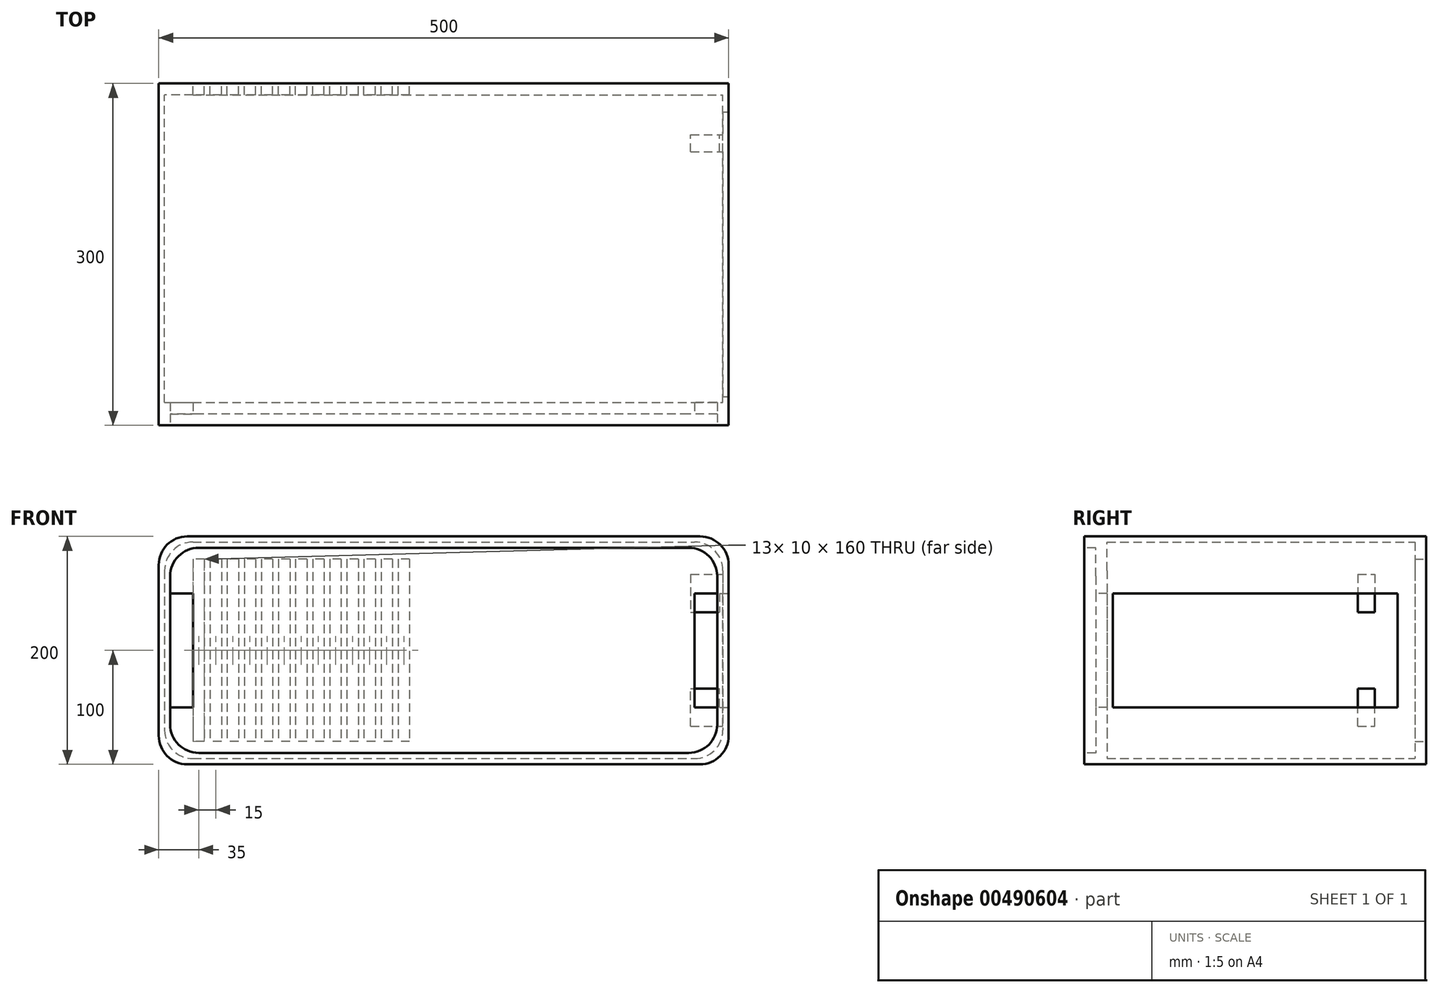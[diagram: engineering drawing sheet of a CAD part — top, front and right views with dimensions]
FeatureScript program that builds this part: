
annotation { "Feature Type Name" : "Feature", "Feature Type Description" : "" }
export const myFeature = defineFeature(function(context is Context, id is Id, definition is map)
    precondition{}
    {
        {
            var Q0;
            Q0=qCreatedBy(makeId("Front.planeOp"),FACE);
            var sketch = newSketch(context, id + "F0", { "sketchPlane" : qUnion([Q0])});
            skLineSegment(sketch, "E0.bottom", {"start": v(250, 100) * mm, "end": v(-250, 100) * mm});
            skLineSegment(sketch, "E0.top", {"start": v(250, -100) * mm, "end": v(-250, -100) * mm});
            skLineSegment(sketch, "E0.left", {"start": v(250, 100) * mm, "end": v(250, -100) * mm});
            skLineSegment(sketch, "E0.right", {"start": v(-250, 100) * mm, "end": v(-250, -100) * mm});
            skPoint(sketch, "E0.middle", {"position": v(0, 0) * mm});
            skSolve(sketch);
        }
        {
            var Q0;
            Q0=makeQuery(id+"F0.imprint","IMPRINT",FACE,{"disambiguationData":[TD([[makeQuery(id+"F0.imprint","IMPRINT",EDGE,{"derivedFrom":sQuery(id+"F0.wireOp",EDGE,"E0.bottom")}),1.0]])]});
            extrude(context, id + "F1", {"entities" : qUnion([Q0]), "endBound" : BoundingType.SYMMETRIC, "oppositeDirection" : true, "depth" : 300 * mm});
        }
        {
            var Q0;
            Q0=makeQuery(id+"F1.opExtrude","SWEPT_EDGE",EDGE,{"disambiguationData":[OSD([sQuery(id+"F0.wireOp",EDGE,"E0.bottom"),sQuery(id+"F0.wireOp",EDGE,"E0.right")])]});
            var Q1;
            Q1=makeQuery(id+"F1.opExtrude","SWEPT_EDGE",EDGE,{"disambiguationData":[OSD([sQuery(id+"F0.wireOp",EDGE,"E0.bottom"),sQuery(id+"F0.wireOp",EDGE,"E0.left")])]});
            var Q2;
            Q2=makeQuery(id+"F1.opExtrude","SWEPT_EDGE",EDGE,{"disambiguationData":[OSD([sQuery(id+"F0.wireOp",EDGE,"E0.top"),sQuery(id+"F0.wireOp",EDGE,"E0.left")])]});
            var Q3;
            Q3=makeQuery(id+"F1.opExtrude","SWEPT_EDGE",EDGE,{"disambiguationData":[OSD([sQuery(id+"F0.wireOp",EDGE,"E0.top"),sQuery(id+"F0.wireOp",EDGE,"E0.right")])]});
            fillet(context, id + "F2", {"entities" : qUnion([Q0, Q1, Q2, Q3]), "radius" : 25 * mm, "tangentPropagation" : true, "allowEdgeOverflow" : false});
        }
        {
            var Q0;
            Q0=makeQuery(id+"F1.opExtrude","CAP_FACE",FACE,{"disambiguationData":[OSD([sQuery(id+"F0.wireOp",EDGE,"E0.bottom"),sQuery(id+"F0.wireOp",EDGE,"E0.top"),sQuery(id+"F0.wireOp",EDGE,"E0.left"),sQuery(id+"F0.wireOp",EDGE,"E0.right")])],"isStart":true});
            var sketch = newSketch(context, id + "F3", { "sketchPlane" : qUnion([Q0])});
            skLineSegment(sketch, "E1.bottom", {"start": v(215, 90) * mm, "end": v(-215, 90) * mm});
            skLineSegment(sketch, "E1.top", {"start": v(215, -90) * mm, "end": v(-215, -90) * mm});
            skLineSegment(sketch, "E1.left", {"start": v(240, 65) * mm, "end": v(240, -65) * mm});
            skLineSegment(sketch, "E1.right", {"start": v(-240, 65) * mm, "end": v(-240, -65) * mm});
            skPoint(sketch, "E1.middle", {"position": v(0, 0) * mm});
            skPoint(sketch, "E2.visualSharp", {"position": v(-240, 90) * mm});
            skArc(sketch, "E2.filletArc", {"start": v(-215, 90) * mm, "mid": v(-232.68, 82.68) * mm, "end": v(-240, 65) * mm});
            skPoint(sketch, "E3.visualSharp", {"position": v(240, 90) * mm});
            skArc(sketch, "E3.filletArc", {"start": v(240, 65) * mm, "mid": v(232.68, 82.68) * mm, "end": v(215, 90) * mm});
            skPoint(sketch, "E4.visualSharp", {"position": v(240, -90) * mm});
            skArc(sketch, "E4.filletArc", {"start": v(215, -90) * mm, "mid": v(232.68, -82.68) * mm, "end": v(240, -65) * mm});
            skPoint(sketch, "E5.visualSharp", {"position": v(-240, -90) * mm});
            skArc(sketch, "E5.filletArc", {"start": v(-240, -65) * mm, "mid": v(-232.68, -82.68) * mm, "end": v(-215, -90) * mm});
            skSolve(sketch);
        }
        {
            var Q0;
            Q0=makeQuery(id+"F3.imprint","IMPRINT",FACE,{"disambiguationData":[TD([[makeQuery(id+"F3.imprint","IMPRINT",EDGE,{"derivedFrom":sQuery(id+"F3.wireOp",EDGE,"E1.bottom")}),1.0]])]});
            extrude(context, id + "F4", {"entities" : qUnion([Q0]), "operationType" : NewBodyOperationType.REMOVE, "oppositeDirection" : true, "depth" : 10 * mm});
        }
        {
            var Q0;
            Q0=makeQuery(id+"F1.opExtrude","CAP_FACE",FACE,{"disambiguationData":[OSD([sQuery(id+"F0.wireOp",EDGE,"E0.bottom"),sQuery(id+"F0.wireOp",EDGE,"E0.top"),sQuery(id+"F0.wireOp",EDGE,"E0.left"),sQuery(id+"F0.wireOp",EDGE,"E0.right")])],"isStart":false});
            var sketch = newSketch(context, id + "F5", { "sketchPlane" : qUnion([Q0])});
            skLineSegment(sketch, "E6.bottom", {"start": v(220, 95) * mm, "end": v(-220, 95) * mm});
            skLineSegment(sketch, "E6.top", {"start": v(220, -95) * mm, "end": v(-220, -95) * mm});
            skLineSegment(sketch, "E6.left", {"start": v(245, 70) * mm, "end": v(245, -70) * mm});
            skLineSegment(sketch, "E6.right", {"start": v(-245, 70) * mm, "end": v(-245, -70) * mm});
            skPoint(sketch, "E6.middle", {"position": v(0, 0) * mm});
            skPoint(sketch, "E7.visualSharp", {"position": v(-245, 95) * mm});
            skArc(sketch, "E7.filletArc", {"start": v(-220, 95) * mm, "mid": v(-237.68, 87.68) * mm, "end": v(-245, 70) * mm});
            skPoint(sketch, "E8.visualSharp", {"position": v(245, 95) * mm});
            skArc(sketch, "E8.filletArc", {"start": v(245, 70) * mm, "mid": v(237.68, 87.68) * mm, "end": v(220, 95) * mm});
            skPoint(sketch, "E9.visualSharp", {"position": v(245, -95) * mm});
            skArc(sketch, "E9.filletArc", {"start": v(220, -95) * mm, "mid": v(237.68, -87.68) * mm, "end": v(245, -70) * mm});
            skPoint(sketch, "E10.visualSharp", {"position": v(-245, -95) * mm});
            skArc(sketch, "E10.filletArc", {"start": v(-245, -70) * mm, "mid": v(-237.68, -87.68) * mm, "end": v(-220, -95) * mm});
            skSolve(sketch);
        }
        {
            var Q0;
            Q0=makeQuery(id+"F5.imprint","IMPRINT",FACE,{"disambiguationData":[TD([[makeQuery(id+"F5.imprint","IMPRINT",EDGE,{"derivedFrom":sQuery(id+"F5.wireOp",EDGE,"E6.bottom")}),1.0]])]});
            extrude(context, id + "F6", {"entities" : qUnion([Q0]), "operationType" : NewBodyOperationType.REMOVE, "oppositeDirection" : true, "depth" : 280 * mm});
        }
        {
            var Q0;
            {var subQ0=sQuery(id+"F3.wireOp",EDGE,"E5.filletArc");var subQ1=sQuery(id+"F3.wireOp",EDGE,"E1.right");var subQ2=sQuery(id+"F3.wireOp",EDGE,"E4.filletArc");var subQ3=sQuery(id+"F3.wireOp",EDGE,"E1.left");var subQ4=sQuery(id+"F3.wireOp",EDGE,"E3.filletArc");var subQ5=sQuery(id+"F3.wireOp",EDGE,"E2.filletArc");var subQ6=sQuery(id+"F3.wireOp",EDGE,"E1.top");var subQ7=sQuery(id+"F3.wireOp",EDGE,"E1.bottom");Q0=makeQuery(id+"FLLnC6cUkQxxpey_1.boolean.opBoolean","SPLIT",FACE,{"disambiguationData":[TD([makeQuery(id+"F4.boolean.opBoolean","COPY",FACE,{"derivedFrom":makeQuery(id+"F4.opExtrude","SWEPT_FACE",FACE,{"disambiguationData":[OSD([subQ7])]})})])],"derivedFrom":makeQuery(id+"F4.boolean.opBoolean","COPY",FACE,{"derivedFrom":makeQuery(id+"F4.opExtrude","CAP_FACE",FACE,{"disambiguationData":[OSD([subQ7,subQ6,subQ3,subQ1,subQ5,subQ4,subQ2,subQ0])],"isStart":false})})});}
            var sketch = newSketch(context, id + "F7", { "sketchPlane" : qUnion([Q0])});
            skLineSegment(sketch, "E11.bottom", {"start": v(240, 50) * mm, "end": v(220, 50) * mm});
            skLineSegment(sketch, "E11.top", {"start": v(240, -50) * mm, "end": v(220, -50) * mm});
            skLineSegment(sketch, "E11.left", {"start": v(240, 50) * mm, "end": v(240, -50) * mm});
            skLineSegment(sketch, "E11.right", {"start": v(220, 50) * mm, "end": v(220, -50) * mm});
            skLineSegment(sketch, "E12.MirrorCS", {"start": v(-240, -50) * mm, "end": v(-220, -50) * mm});
            skLineSegment(sketch, "E13.MirrorCS", {"start": v(-240, 50) * mm, "end": v(-220, 50) * mm});
            skLineSegment(sketch, "E14.MirrorCS", {"start": v(-240, 50) * mm, "end": v(-240, -50) * mm});
            skLineSegment(sketch, "E15.MirrorCS", {"start": v(-220, 50) * mm, "end": v(-220, -50) * mm});
            skSolve(sketch);
        }
        {
            var Q0;
            Q0=makeQuery(id+"F7.imprint","IMPRINT",FACE,{"disambiguationData":[TD([[makeQuery(id+"F7.imprint","IMPRINT",EDGE,{"derivedFrom":sQuery(id+"F7.wireOp",EDGE,"E12.MirrorCS")}),1.0]])]});
            var Q1;
            Q1=makeQuery(id+"F7.imprint","IMPRINT",FACE,{"disambiguationData":[TD([[makeQuery(id+"F7.imprint","IMPRINT",EDGE,{"derivedFrom":sQuery(id+"F7.wireOp",EDGE,"E11.bottom")}),1.0]])]});
            extrude(context, id + "F8", {"entities" : qUnion([Q0, Q1]), "operationType" : NewBodyOperationType.REMOVE, "endBound" : BoundingType.UP_TO_NEXT, "oppositeDirection" : true, "depth" : 25 * mm});
        }
        {
            var Q0;
            Q0=makeQuery(id+"F1.opExtrude","SWEPT_FACE",FACE,{"disambiguationData":[OSD([sQuery(id+"F0.wireOp",EDGE,"E0.bottom")])]});
            var sketch = newSketch(context, id + "F9", { "sketchPlane" : qUnion([Q0])});
            skLineSegment(sketch, "E16.bottom", {"start": v(-250, 140) * mm, "end": v(250, 140) * mm});
            skLineSegment(sketch, "E16.left", {"start": v(-250, 140) * mm, "end": v(-250, 150) * mm});
            skLineSegment(sketch, "E16.right", {"start": v(250, 140) * mm, "end": v(250, 150) * mm});
            skPoint(sketch, "E16.middle", {"position": v(0, 150) * mm});
            skLineSegment(sketch, "E17", {"start": v(-250, 150) * mm, "end": v(250, 150) * mm});
            skSolve(sketch);
        }
        {
            var Q0;
            {var subQ0=sQuery(id+"F9.wireOp",EDGE,"E16.left");Q0=makeQuery(id+"F9.imprint","IMPRINT",FACE,{"disambiguationData":[TD([[makeQuery(id+"F9.imprint","IMPRINT",EDGE,{"derivedFrom":subQ0}),-1.0]])]});}
            var Q1;
            {var subQ0=sQuery(id+"F9.wireOp",EDGE,"E16.bottom");var subQ1=sQuery(id+"F0.wireOp",EDGE,"E0.bottom");var subQ2=makeQuery(id+"F1.opExtrude","SWEPT_FACE",FACE,{"disambiguationData":[OSD([subQ1])]});var subQ3=makeQuery(id+"F2.opFillet","BLEND_EDGE",EDGE,{"blendedFrom":[makeQuery(id+"F1.opExtrude","SWEPT_EDGE",EDGE,{"disambiguationData":[OSD([subQ1,sQuery(id+"F0.wireOp",EDGE,"E0.right")])]}),subQ2],"blendedInto":[subQ2]});var subQ4=makeQuery(id+"F9.imprint","INTERSECT",VERTEX,{"derivedFrom":[subQ3,subQ0]});Q1=makeQuery(id+"F9.imprint","IMPRINT",FACE,{"disambiguationData":[TD([[makeQuery(id+"F9.imprint","IMPRINT",EDGE,{"disambiguationData":[TD([[subQ4,-1.0]])],"derivedFrom":subQ0}),1.0]])]});}
            var Q2;
            {var subQ0=sQuery(id+"F9.wireOp",EDGE,"E16.right");Q2=makeQuery(id+"F9.imprint","IMPRINT",FACE,{"disambiguationData":[TD([[makeQuery(id+"F9.imprint","IMPRINT",EDGE,{"derivedFrom":subQ0}),1.0]])]});}
            var Q3;
            Q3=makeQuery(id+"F1.opExtrude","SWEPT_FACE",FACE,{"disambiguationData":[OSD([sQuery(id+"F0.wireOp",EDGE,"E0.top")])]});
            extrude(context, id + "F10", {"entities" : qUnion([Q0, Q1, Q2]), "operationType" : NewBodyOperationType.ADD, "endBound" : BoundingType.UP_TO_SURFACE, "oppositeDirection" : true, "endBoundEntityFace" : qUnion([Q3]), "depth" : 25 * mm});
        }
        {
            var Q0;
            Q0=makeQuery(id+"F10.opExtrude","CAP_EDGE",EDGE,{"disambiguationData":[OSD([sQuery(id+"F9.wireOp",EDGE,"E16.left")])],"isStart":true});
            var Q1;
            Q1=makeQuery(id+"F10.opExtrude","CAP_EDGE",EDGE,{"disambiguationData":[OSD([sQuery(id+"F9.wireOp",EDGE,"E16.left")])],"isStart":false});
            var Q2;
            Q2=makeQuery(id+"F10.opExtrude","CAP_EDGE",EDGE,{"disambiguationData":[OSD([sQuery(id+"F9.wireOp",EDGE,"E16.right")])],"isStart":true});
            var Q3;
            Q3=makeQuery(id+"F10.opExtrude","CAP_EDGE",EDGE,{"disambiguationData":[OSD([sQuery(id+"F9.wireOp",EDGE,"E16.right")])],"isStart":false});
            fillet(context, id + "F11", {"entities" : qUnion([Q0, Q1, Q2, Q3]), "radius" : 25 * mm, "tangentPropagation" : true, "allowEdgeOverflow" : false});
        }
        {
            var Q0;
            Q0=makeQuery(id+"F10.boolean.opBoolean","MERGE",FACE,{"derivedFrom":[makeQuery(id+"F1.opExtrude","SWEPT_FACE",FACE,{"disambiguationData":[OSD([sQuery(id+"F0.wireOp",EDGE,"E0.left")])]}),makeQuery(id+"F10.opExtrude","SWEPT_FACE",FACE,{"disambiguationData":[OSD([sQuery(id+"F9.wireOp",EDGE,"E16.right")])]})]});
            var sketch = newSketch(context, id + "F12", { "sketchPlane" : qUnion([Q0])});
            skLineSegment(sketch, "E18.bottom", {"start": v(-125, 50) * mm, "end": v(125, 50) * mm});
            skLineSegment(sketch, "E18.top", {"start": v(-125, -50) * mm, "end": v(125, -50) * mm});
            skLineSegment(sketch, "E18.left", {"start": v(-125, 50) * mm, "end": v(-125, -50) * mm});
            skLineSegment(sketch, "E18.right", {"start": v(125, 50) * mm, "end": v(125, -50) * mm});
            skSolve(sketch);
        }
        {
            var Q0;
            Q0=makeQuery(id+"F12.imprint","IMPRINT",FACE,{"disambiguationData":[TD([[makeQuery(id+"F12.imprint","IMPRINT",EDGE,{"derivedFrom":sQuery(id+"F12.wireOp",EDGE,"E18.bottom")}),-1.0]])]});
            extrude(context, id + "F13", {"entities" : qUnion([Q0]), "operationType" : NewBodyOperationType.REMOVE, "endBound" : BoundingType.UP_TO_NEXT, "oppositeDirection" : true, "depth" : 25 * mm});
        }
        {
            var Q0;
            Q0=makeQuery(id+"F10.boolean.opBoolean","MERGE",FACE,{"derivedFrom":[makeQuery(id+"F1.opExtrude","CAP_FACE",FACE,{"disambiguationData":[OSD([sQuery(id+"F0.wireOp",EDGE,"E0.bottom"),sQuery(id+"F0.wireOp",EDGE,"E0.top"),sQuery(id+"F0.wireOp",EDGE,"E0.left"),sQuery(id+"F0.wireOp",EDGE,"E0.right")])],"isStart":false}),makeQuery(id+"F10.opExtrude","SWEPT_FACE",FACE,{"disambiguationData":[OSD([sQuery(id+"F9.wireOp",EDGE,"E17")])]})]});
            var sketch = newSketch(context, id + "F14", { "sketchPlane" : qUnion([Q0])});
            skLineSegment(sketch, "E19.bottom", {"start": v(30, 80) * mm, "end": v(40, 80) * mm});
            skLineSegment(sketch, "E19.top", {"start": v(30, -80) * mm, "end": v(40, -80) * mm});
            skLineSegment(sketch, "E19.left", {"start": v(30, 80) * mm, "end": v(30, -80) * mm});
            skLineSegment(sketch, "E20", {"start": v(40, 80) * mm, "end": v(40, -80) * mm});
            skLineSegment(sketch, "E21.1.0.0", {"start": v(45, 80) * mm, "end": v(45, -80) * mm});
            skLineSegment(sketch, "E21.1.0.1", {"start": v(45, 80) * mm, "end": v(55, 80) * mm});
            skLineSegment(sketch, "E21.1.0.2", {"start": v(55, 80) * mm, "end": v(55, -80) * mm});
            skLineSegment(sketch, "E21.1.0.3", {"start": v(45, -80) * mm, "end": v(55, -80) * mm});
            skLineSegment(sketch, "E21.2.0.0", {"start": v(60, 80) * mm, "end": v(60, -80) * mm});
            skLineSegment(sketch, "E21.2.0.1", {"start": v(60, 80) * mm, "end": v(70, 80) * mm});
            skLineSegment(sketch, "E21.2.0.2", {"start": v(70, 80) * mm, "end": v(70, -80) * mm});
            skLineSegment(sketch, "E21.2.0.3", {"start": v(60, -80) * mm, "end": v(70, -80) * mm});
            skLineSegment(sketch, "E21.3.0.0", {"start": v(75, 80) * mm, "end": v(75, -80) * mm});
            skLineSegment(sketch, "E21.3.0.1", {"start": v(75, 80) * mm, "end": v(85, 80) * mm});
            skLineSegment(sketch, "E21.3.0.2", {"start": v(85, 80) * mm, "end": v(85, -80) * mm});
            skLineSegment(sketch, "E21.3.0.3", {"start": v(75, -80) * mm, "end": v(85, -80) * mm});
            skLineSegment(sketch, "E21.4.0.0", {"start": v(90, 80) * mm, "end": v(90, -80) * mm});
            skLineSegment(sketch, "E21.4.0.1", {"start": v(90, 80) * mm, "end": v(100, 80) * mm});
            skLineSegment(sketch, "E21.4.0.2", {"start": v(100, 80) * mm, "end": v(100, -80) * mm});
            skLineSegment(sketch, "E21.4.0.3", {"start": v(90, -80) * mm, "end": v(100, -80) * mm});
            skLineSegment(sketch, "E21.5.0.0", {"start": v(105, 80) * mm, "end": v(105, -80) * mm});
            skLineSegment(sketch, "E21.5.0.1", {"start": v(105, 80) * mm, "end": v(115, 80) * mm});
            skLineSegment(sketch, "E21.5.0.2", {"start": v(115, 80) * mm, "end": v(115, -80) * mm});
            skLineSegment(sketch, "E21.5.0.3", {"start": v(105, -80) * mm, "end": v(115, -80) * mm});
            skLineSegment(sketch, "E21.6.0.0", {"start": v(120, 80) * mm, "end": v(120, -80) * mm});
            skLineSegment(sketch, "E21.6.0.1", {"start": v(120, 80) * mm, "end": v(130, 80) * mm});
            skLineSegment(sketch, "E21.6.0.2", {"start": v(130, 80) * mm, "end": v(130, -80) * mm});
            skLineSegment(sketch, "E21.6.0.3", {"start": v(120, -80) * mm, "end": v(130, -80) * mm});
            skLineSegment(sketch, "E21.7.0.0", {"start": v(135, 80) * mm, "end": v(135, -80) * mm});
            skLineSegment(sketch, "E21.7.0.1", {"start": v(135, 80) * mm, "end": v(145, 80) * mm});
            skLineSegment(sketch, "E21.7.0.2", {"start": v(145, 80) * mm, "end": v(145, -80) * mm});
            skLineSegment(sketch, "E21.7.0.3", {"start": v(135, -80) * mm, "end": v(145, -80) * mm});
            skLineSegment(sketch, "E21.8.0.0", {"start": v(150, 80) * mm, "end": v(150, -80) * mm});
            skLineSegment(sketch, "E21.8.0.1", {"start": v(150, 80) * mm, "end": v(160, 80) * mm});
            skLineSegment(sketch, "E21.8.0.2", {"start": v(160, 80) * mm, "end": v(160, -80) * mm});
            skLineSegment(sketch, "E21.8.0.3", {"start": v(150, -80) * mm, "end": v(160, -80) * mm});
            skLineSegment(sketch, "E21.9.0.0", {"start": v(165, 80) * mm, "end": v(165, -80) * mm});
            skLineSegment(sketch, "E21.9.0.1", {"start": v(165, 80) * mm, "end": v(175, 80) * mm});
            skLineSegment(sketch, "E21.9.0.2", {"start": v(175, 80) * mm, "end": v(175, -80) * mm});
            skLineSegment(sketch, "E21.9.0.3", {"start": v(165, -80) * mm, "end": v(175, -80) * mm});
            skLineSegment(sketch, "E21.10.0.0", {"start": v(180, 80) * mm, "end": v(180, -80) * mm});
            skLineSegment(sketch, "E21.10.0.1", {"start": v(180, 80) * mm, "end": v(190, 80) * mm});
            skLineSegment(sketch, "E21.10.0.2", {"start": v(190, 80) * mm, "end": v(190, -80) * mm});
            skLineSegment(sketch, "E21.10.0.3", {"start": v(180, -80) * mm, "end": v(190, -80) * mm});
            skLineSegment(sketch, "E21.11.0.0", {"start": v(195, 80) * mm, "end": v(195, -80) * mm});
            skLineSegment(sketch, "E21.11.0.1", {"start": v(195, 80) * mm, "end": v(205, 80) * mm});
            skLineSegment(sketch, "E21.11.0.2", {"start": v(205, 80) * mm, "end": v(205, -80) * mm});
            skLineSegment(sketch, "E21.11.0.3", {"start": v(195, -80) * mm, "end": v(205, -80) * mm});
            skLineSegment(sketch, "E21.12.0.0", {"start": v(210, 80) * mm, "end": v(210, -80) * mm});
            skLineSegment(sketch, "E21.12.0.1", {"start": v(210, 80) * mm, "end": v(220, 80) * mm});
            skLineSegment(sketch, "E21.12.0.2", {"start": v(220, 80) * mm, "end": v(220, -80) * mm});
            skLineSegment(sketch, "E21.12.0.3", {"start": v(210, -80) * mm, "end": v(220, -80) * mm});
            skLineSegment(sketch, "E21.direction1", {"start": v(30, -80) * mm, "end": v(45, -80) * mm, "construction": true});
            skSolve(sketch);
        }
        {
            var Q0;
            Q0=makeQuery(id+"F14.imprint","IMPRINT",FACE,{"disambiguationData":[TD([[makeQuery(id+"F14.imprint","IMPRINT",EDGE,{"derivedFrom":sQuery(id+"F14.wireOp",EDGE,"E19.bottom")}),-1.0]])]});
            var Q1;
            Q1=makeQuery(id+"F14.imprint","IMPRINT",FACE,{"disambiguationData":[TD([[makeQuery(id+"F14.imprint","IMPRINT",EDGE,{"derivedFrom":sQuery(id+"F14.wireOp",EDGE,"E21.1.0.0")}),1.0]])]});
            var Q2;
            Q2=makeQuery(id+"F14.imprint","IMPRINT",FACE,{"disambiguationData":[TD([[makeQuery(id+"F14.imprint","IMPRINT",EDGE,{"derivedFrom":sQuery(id+"F14.wireOp",EDGE,"E21.2.0.0")}),1.0]])]});
            var Q3;
            Q3=makeQuery(id+"F14.imprint","IMPRINT",FACE,{"disambiguationData":[TD([[makeQuery(id+"F14.imprint","IMPRINT",EDGE,{"derivedFrom":sQuery(id+"F14.wireOp",EDGE,"E21.3.0.0")}),1.0]])]});
            var Q4;
            Q4=makeQuery(id+"F14.imprint","IMPRINT",FACE,{"disambiguationData":[TD([[makeQuery(id+"F14.imprint","IMPRINT",EDGE,{"derivedFrom":sQuery(id+"F14.wireOp",EDGE,"E21.4.0.0")}),1.0]])]});
            var Q5;
            Q5=makeQuery(id+"F14.imprint","IMPRINT",FACE,{"disambiguationData":[TD([[makeQuery(id+"F14.imprint","IMPRINT",EDGE,{"derivedFrom":sQuery(id+"F14.wireOp",EDGE,"E21.5.0.0")}),1.0]])]});
            var Q6;
            Q6=makeQuery(id+"F14.imprint","IMPRINT",FACE,{"disambiguationData":[TD([[makeQuery(id+"F14.imprint","IMPRINT",EDGE,{"derivedFrom":sQuery(id+"F14.wireOp",EDGE,"E21.6.0.0")}),1.0]])]});
            var Q7;
            Q7=makeQuery(id+"F14.imprint","IMPRINT",FACE,{"disambiguationData":[TD([[makeQuery(id+"F14.imprint","IMPRINT",EDGE,{"derivedFrom":sQuery(id+"F14.wireOp",EDGE,"E21.7.0.0")}),1.0]])]});
            var Q8;
            Q8=makeQuery(id+"F14.imprint","IMPRINT",FACE,{"disambiguationData":[TD([[makeQuery(id+"F14.imprint","IMPRINT",EDGE,{"derivedFrom":sQuery(id+"F14.wireOp",EDGE,"E21.8.0.0")}),1.0]])]});
            var Q9;
            Q9=makeQuery(id+"F14.imprint","IMPRINT",FACE,{"disambiguationData":[TD([[makeQuery(id+"F14.imprint","IMPRINT",EDGE,{"derivedFrom":sQuery(id+"F14.wireOp",EDGE,"E21.9.0.0")}),1.0]])]});
            var Q10;
            Q10=makeQuery(id+"F14.imprint","IMPRINT",FACE,{"disambiguationData":[TD([[makeQuery(id+"F14.imprint","IMPRINT",EDGE,{"derivedFrom":sQuery(id+"F14.wireOp",EDGE,"E21.10.0.0")}),1.0]])]});
            var Q11;
            Q11=makeQuery(id+"F14.imprint","IMPRINT",FACE,{"disambiguationData":[TD([[makeQuery(id+"F14.imprint","IMPRINT",EDGE,{"derivedFrom":sQuery(id+"F14.wireOp",EDGE,"E21.11.0.0")}),1.0]])]});
            var Q12;
            Q12=makeQuery(id+"F14.imprint","IMPRINT",FACE,{"disambiguationData":[TD([[makeQuery(id+"F14.imprint","IMPRINT",EDGE,{"derivedFrom":sQuery(id+"F14.wireOp",EDGE,"E21.12.0.0")}),1.0]])]});
            var Q13;
            Q13=makeQuery(id+"F14.imprint","IMPRINT",FACE,{"disambiguationData":[TD([[makeQuery(id+"F14.imprint","IMPRINT",EDGE,{"derivedFrom":sQuery(id+"F14.wireOp",EDGE,"E21.13.0.0")}),1.0]])]});
            var Q14;
            Q14=makeQuery(id+"F14.imprint","IMPRINT",FACE,{"disambiguationData":[TD([[makeQuery(id+"F14.imprint","IMPRINT",EDGE,{"derivedFrom":sQuery(id+"F14.wireOp",EDGE,"E21.14.0.0")}),1.0]])]});
            var Q15;
            Q15=makeQuery(id+"F14.imprint","IMPRINT",FACE,{"disambiguationData":[TD([[makeQuery(id+"F14.imprint","IMPRINT",EDGE,{"derivedFrom":sQuery(id+"F14.wireOp",EDGE,"E21.15.0.0")}),1.0]])]});
            var Q16;
            Q16=makeQuery(id+"F14.imprint","IMPRINT",FACE,{"disambiguationData":[TD([[makeQuery(id+"F14.imprint","IMPRINT",EDGE,{"derivedFrom":sQuery(id+"F14.wireOp",EDGE,"E21.16.0.0")}),1.0]])]});
            var Q17;
            Q17=makeQuery(id+"F14.imprint","IMPRINT",FACE,{"disambiguationData":[TD([[makeQuery(id+"F14.imprint","IMPRINT",EDGE,{"derivedFrom":sQuery(id+"F14.wireOp",EDGE,"E21.17.0.0")}),1.0]])]});
            var Q18;
            Q18=makeQuery(id+"F14.imprint","IMPRINT",FACE,{"disambiguationData":[TD([[makeQuery(id+"F14.imprint","IMPRINT",EDGE,{"derivedFrom":sQuery(id+"F14.wireOp",EDGE,"E21.18.0.0")}),1.0]])]});
            var Q19;
            Q19=makeQuery(id+"F14.imprint","IMPRINT",FACE,{"disambiguationData":[TD([[makeQuery(id+"F14.imprint","IMPRINT",EDGE,{"derivedFrom":sQuery(id+"F14.wireOp",EDGE,"E21.19.0.0")}),1.0]])]});
            extrude(context, id + "F15", {"entities" : qUnion([Q0, Q1, Q2, Q3, Q4, Q5, Q6, Q7, Q8, Q9, Q10, Q11, Q12, Q13, Q14, Q15, Q16, Q17, Q18, Q19]), "operationType" : NewBodyOperationType.REMOVE, "endBound" : BoundingType.UP_TO_NEXT, "oppositeDirection" : true, "depth" : 25 * mm, "offsetDistance" : 25 * mm});
        }
        {
            var Q0;
            Q0=makeQuery(id+"F10.boolean.opBoolean","MERGE",FACE,{"derivedFrom":[makeQuery(id+"F1.opExtrude","SWEPT_FACE",FACE,{"disambiguationData":[OSD([sQuery(id+"F0.wireOp",EDGE,"E0.left")])]}),makeQuery(id+"F10.opExtrude","SWEPT_FACE",FACE,{"disambiguationData":[OSD([sQuery(id+"F9.wireOp",EDGE,"E16.right")])]})]});
            var sketch = newSketch(context, id + "F16", { "sketchPlane" : qUnion([Q0])});
            skLineSegment(sketch, "E22.bottom", {"start": v(90, 66.75) * mm, "end": v(105, 66.75) * mm});
            skLineSegment(sketch, "E22.top", {"start": v(90, 33.45) * mm, "end": v(105, 33.45) * mm});
            skLineSegment(sketch, "E22.left", {"start": v(90, 66.75) * mm, "end": v(90, 33.45) * mm});
            skLineSegment(sketch, "E22.right", {"start": v(105, 66.75) * mm, "end": v(105, 33.45) * mm});
            skLineSegment(sketch, "E23.MirrorCS", {"start": v(90, -66.75) * mm, "end": v(105, -66.75) * mm});
            skLineSegment(sketch, "E24.MirrorCS", {"start": v(90, -33.45) * mm, "end": v(105, -33.45) * mm});
            skLineSegment(sketch, "E25.MirrorCS", {"start": v(90, -66.75) * mm, "end": v(90, -33.45) * mm});
            skLineSegment(sketch, "E26.MirrorCS", {"start": v(105, -66.75) * mm, "end": v(105, -33.45) * mm});
            skSolve(sketch);
        }
        {
            var Q0;
            {var subQ0=sQuery(id+"F16.wireOp",EDGE,"E22.bottom");Q0=makeQuery(id+"F16.imprint","IMPRINT",FACE,{"disambiguationData":[TD([[makeQuery(id+"F16.imprint","IMPRINT",EDGE,{"derivedFrom":subQ0}),-1.0]])]});}
            var Q1;
            {var subQ0=sQuery(id+"F16.wireOp",EDGE,"E22.top");Q1=makeQuery(id+"F16.imprint","IMPRINT",FACE,{"disambiguationData":[TD([[makeQuery(id+"F16.imprint","IMPRINT",EDGE,{"derivedFrom":subQ0}),1.0]])]});}
            var Q2;
            {var subQ0=sQuery(id+"F16.wireOp",EDGE,"E24.MirrorCS");Q2=makeQuery(id+"F16.imprint","IMPRINT",FACE,{"disambiguationData":[TD([[makeQuery(id+"F16.imprint","IMPRINT",EDGE,{"derivedFrom":subQ0}),-1.0]])]});}
            var Q3;
            {var subQ0=sQuery(id+"F16.wireOp",EDGE,"E23.MirrorCS");Q3=makeQuery(id+"F16.imprint","IMPRINT",FACE,{"disambiguationData":[TD([[makeQuery(id+"F16.imprint","IMPRINT",EDGE,{"derivedFrom":subQ0}),1.0]])]});}
            extrude(context, id + "F17", {"entities" : qUnion([Q0, Q1, Q2, Q3]), "operationType" : NewBodyOperationType.ADD, "oppositeDirection" : true, "depth" : 33.3 * mm, "offsetDistance" : 25 * mm});
        }
        {
            var Q0;
            Q0=makeQuery(id+"F17.boolean.opBoolean","MERGE",FACE,{"derivedFrom":[makeQuery(id+"F10.boolean.opBoolean","MERGE",FACE,{"derivedFrom":[makeQuery(id+"F1.opExtrude","SWEPT_FACE",FACE,{"disambiguationData":[OSD([sQuery(id+"F0.wireOp",EDGE,"E0.left")])]}),makeQuery(id+"F10.opExtrude","SWEPT_FACE",FACE,{"disambiguationData":[OSD([sQuery(id+"F9.wireOp",EDGE,"E16.right")])]})]}),makeQuery(id+"F17.opExtrude","CAP_FACE",FACE,{"disambiguationData":[OSD([sQuery(id+"F16.wireOp",EDGE,"E22.bottom"),sQuery(id+"F16.wireOp",EDGE,"E22.top"),sQuery(id+"F16.wireOp",EDGE,"E22.left"),sQuery(id+"F16.wireOp",EDGE,"E22.right")])],"isStart":true}),makeQuery(id+"F17.opExtrude","CAP_FACE",FACE,{"disambiguationData":[OSD([sQuery(id+"F16.wireOp",EDGE,"E23.MirrorCS"),sQuery(id+"F16.wireOp",EDGE,"E24.MirrorCS"),sQuery(id+"F16.wireOp",EDGE,"E25.MirrorCS"),sQuery(id+"F16.wireOp",EDGE,"E26.MirrorCS")])],"isStart":true})]});
            var sketch = newSketch(context, id + "F18", { "sketchPlane" : qUnion([Q0])});
            skLineSegment(sketch, "E27.bottom", {"start": v(90, 50) * mm, "end": v(105, 50) * mm});
            skLineSegment(sketch, "E27.top", {"start": v(90, 33.45) * mm, "end": v(105, 33.45) * mm});
            skLineSegment(sketch, "E27.left", {"start": v(90, 50) * mm, "end": v(90, 33.45) * mm});
            skLineSegment(sketch, "E27.right", {"start": v(105, 50) * mm, "end": v(105, 33.45) * mm});
            skLineSegment(sketch, "E28.bottom", {"start": v(90, -33.45) * mm, "end": v(105, -33.45) * mm});
            skLineSegment(sketch, "E28.top", {"start": v(90, -50) * mm, "end": v(105, -50) * mm});
            skLineSegment(sketch, "E28.left", {"start": v(90, -33.45) * mm, "end": v(90, -50) * mm});
            skLineSegment(sketch, "E28.right", {"start": v(105, -33.45) * mm, "end": v(105, -50) * mm});
            skSolve(sketch);
        }
        {
            var Q0;
            Q0=makeQuery(id+"F18.imprint","IMPRINT",FACE,{"disambiguationData":[TD([[makeQuery(id+"F18.imprint","IMPRINT",EDGE,{"derivedFrom":sQuery(id+"F18.wireOp",EDGE,"E27.bottom")}),-1.0]])]});
            var Q1;
            Q1=makeQuery(id+"F18.imprint","IMPRINT",FACE,{"disambiguationData":[TD([[makeQuery(id+"F18.imprint","IMPRINT",EDGE,{"derivedFrom":sQuery(id+"F18.wireOp",EDGE,"E28.bottom")}),-1.0]])]});
            extrude(context, id + "F19", {"entities" : qUnion([Q0, Q1]), "operationType" : NewBodyOperationType.REMOVE, "oppositeDirection" : true, "depth" : 8 * mm, "offsetDistance" : 25 * mm});
        }
    });
